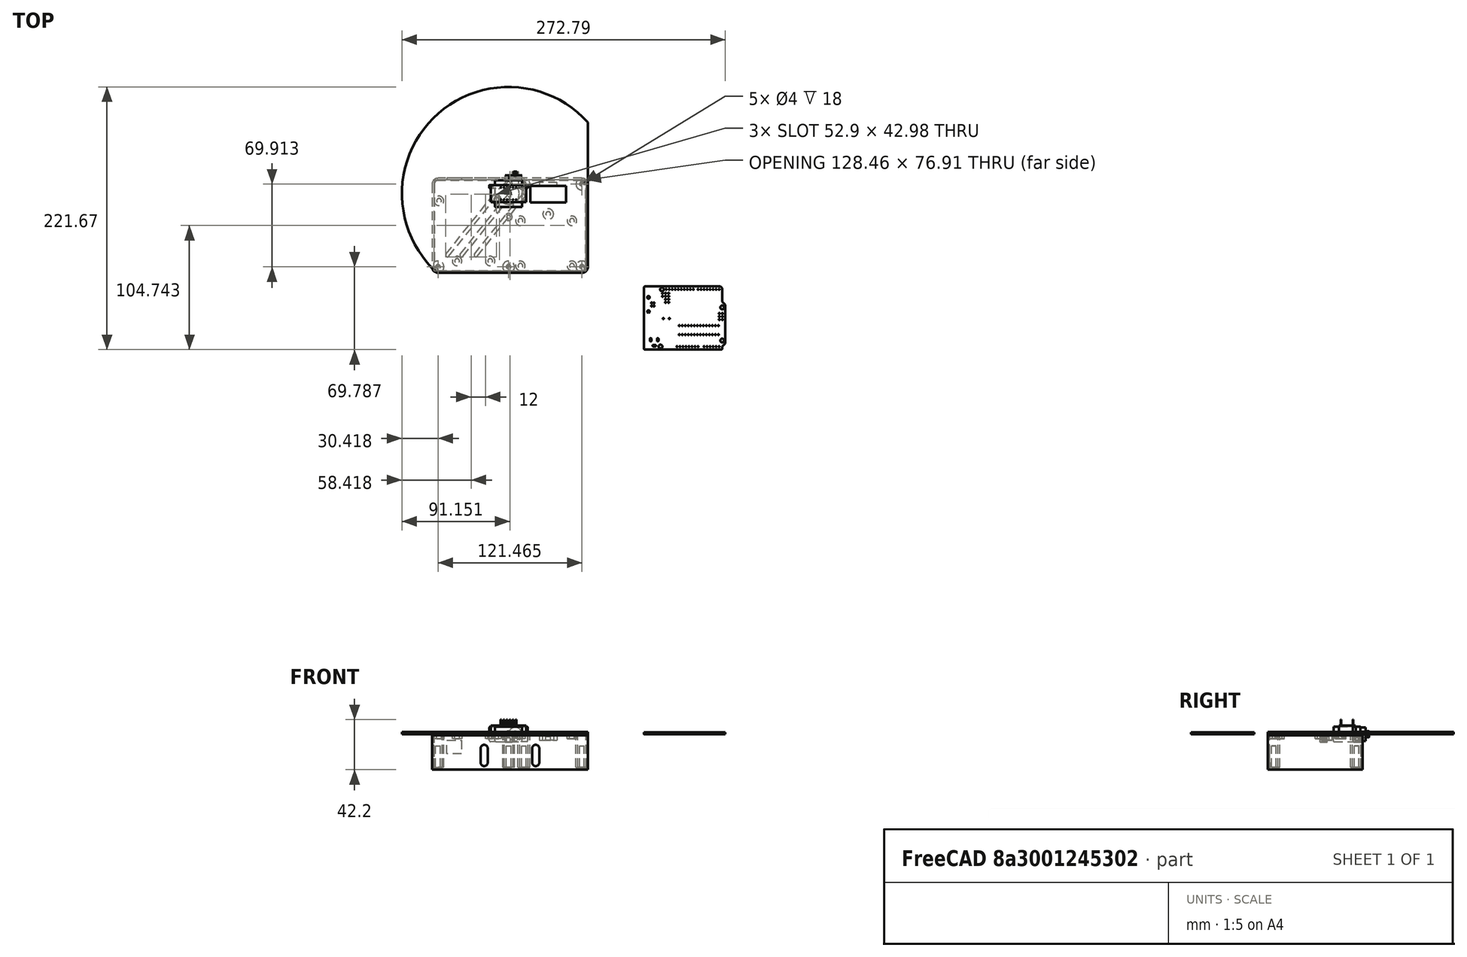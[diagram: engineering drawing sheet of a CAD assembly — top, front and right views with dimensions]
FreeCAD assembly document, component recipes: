
FREECAD ASSEMBLY — COMPONENT RECIPES ("shell")

This assembly document has 4 components, labeled P0..P3 below (a component is one placed body or linked part). 1 of them carries a construction recipe — the FreeCAD feature program that regenerates the part from scratch, quoted from this document or its linked companion documents; the rest are supplied as boundary geometry only. No exploded tour is included for this assembly.
COMPONENT P0 — geometry summary ("Corps001"; no construction recipe available for this part):
  bounding box: 30.0 x 14.0 x 12.2 mm
  tessellated surface: 924 triangles
  volume: 3034 mm^3 (59% of its bounding box)
  symmetry: 2-fold rotationally symmetric about the z axis; mirror-symmetric across its x mid-plane, y mid-plane
COMPONENT P1 — geometry summary ("SG90-SERVO001"; no construction recipe available for this part):
  bounding box: 32.2 x 29.8 x 12.5 mm
  tessellated surface: 14,478 triangles
  volume: 7213 mm^3 (60% of its bounding box)
  symmetry: mirror-symmetric across its x mid-plane
COMPONENT P2 — geometry summary ("UNO-TH_Rev3e_PCB001"; no construction recipe available for this part):
  bounding box: 68.7 x 53.6 x 1.5 mm
  tessellated surface: 16,748 triangles
  volume: 5303 mm^3 (95% of its bounding box)
  symmetry: mirror-symmetric across its z mid-plane
COMPONENT P3 — recipe-attached ("shell001", modeled in this document).
Construction recipe (the document's own serialized feature program — sketch geometry with constraints, then the solid features built on it; lengths are millimeters unless a unit is written):

FEATURE [Sketcher::SketchObject] Sketch
  ArcFitTolerance = 1e-06
  AttachmentSupport = -> [XY_Plane]
  FullyConstrained = true
  MakeInternals = false
  MapMode = 5
  sketch-geometry (14):
    g0: LineSegment StartX=18.4415 StartY=6.5 StartZ=0 EndX=18.4415 EndY=-7.5 EndZ=0
    g1: LineSegment StartX=18.4415 StartY=-7.5 StartZ=0 EndX=48.4415 EndY=-7.5 EndZ=0
    g2: LineSegment StartX=48.4415 StartY=-7.5 StartZ=0 EndX=48.4415 EndY=6.5 EndZ=0
    g3: LineSegment StartX=48.4415 StartY=6.5 StartZ=0 EndX=18.4415 EndY=6.5 EndZ=0
    g4: GeomPoint [constr] X=33.4415 Y=-0.5 Z=0
    g5: ArcOfCircle CenterX=0 CenterY=0 CenterZ=0 NormalX=0 NormalY=0 NormalZ=1 AngleXU=0 Radius=90 StartAngle=0.733038 EndAngle=3.97935
    g6: Circle CenterX=0 CenterY=0 CenterZ=0 NormalX=0 NormalY=0 NormalZ=1 AngleXU=0 Radius=2.5
    g7: LineSegment [constr] StartX=0 StartY=0 StartZ=0 EndX=66.883 EndY=60.2218 EndZ=0
    g8: LineSegment [constr] StartX=0 StartY=0 StartZ=0 EndX=-60.2218 EndY=-66.883 EndZ=0
    g9: LineSegment StartX=66.883 StartY=60.2218 StartZ=0 EndX=66.883 EndY=-61.883 EndZ=0
    g10: LineSegment StartX=61.883 StartY=-66.883 StartZ=0 EndX=-60.2218 EndY=-66.883 EndZ=0
    g11: ArcOfCircle CenterX=61.883 CenterY=-61.883 CenterZ=0 NormalX=0 NormalY=0 NormalZ=1 AngleXU=0 Radius=5 StartAngle=4.71239 EndAngle=6.28319
    g12: LineSegment [constr] StartX=48.4415 StartY=3.78 StartZ=0 EndX=66.883 EndY=3.78 EndZ=0
    g13: LineSegment [constr] StartX=0 StartY=0 StartZ=0 EndX=18.4415 EndY=0 EndZ=0
  constraints (37):
    c: Coincident(g0,g1)
    c: Coincident(g1,g2)
    c: Coincident(g2,g3)
    c: Coincident(g3,g0)
    c: Vertical(g2)
    c: Horizontal(g1)
    c: Horizontal(g3)
    c: Symmetric(g2,g0,g4)
    c: DistanceX(g1,g1) = 30
    c: DistanceY(g2,g2) = 14
    c: Radius(g5) = 90
    c: Coincident(g5,g-1)
    c: Coincident(g6,g5)
    c: Diameter(g6) = 5
    c: Coincident(g7,g5)
    c: Coincident(g8,g5)
    c: Angle(g8,g-1,g5) = 2.30383
    c: Vertical(g9)
    c: Horizontal(g10)
    c: Angle(g-1,g7) = 0.733038
    c: Tangent(g9,g11) = 1.5708
    c: Tangent(g10,g11) = 1.5708
    c: Radius(g11) = 5
    c: Coincident(g5,g8)
    c: Coincident(g5,g7)
    c: Coincident(g9,g5)
    c: Coincident(g10,g5)
    c: PointOnObject(g12,g9)
    c: PointOnObject(g12,g2)
    c: DistanceY(g-1,g12) = 3.78
    c: Horizontal(g12,g12)
    c: Coincident(g13,g5)
    c: Vertical(g13,g0)
    c: PointOnObject(g13,g-1)
    c: Equal(g12,g13)
    c: Perpendicular(g0,g1)
    c: DistanceY(g-1,g4) = -0.5
FEATURE [PartDesign::Pad] Pad  label="BaseFace"
  Direction = (0,0,1)
  Length = 2
  Length2 = 10
  Profile = -> Sketch
  ReferenceAxis = -> Sketch [N_Axis]
  Refine = true
  Suppressed = false
  Type = 0
FEATURE [Sketcher::SketchObject] Sketch001
  ArcFitTolerance = 1e-06
  AttachmentSupport = -> [XY_Plane]
  FullyConstrained = true
  MakeInternals = false
  MapMode = 2
  sketch-geometry (1):
    g0: Circle CenterX=0 CenterY=0 CenterZ=0 NormalX=0 NormalY=0 NormalZ=1 AngleXU=0 Radius=9
  constraints (2):
    c: Diameter(g0) = 18
    c: Coincident(g0,g-1)
FEATURE [Sketcher::SketchObject] Sketch003
  ArcFitTolerance = 1e-06
  AttachmentOffset = pos=(0,0,2) rot=(0,0,1;0rad)
  AttachmentSupport = -> [XY_Plane]
  FullyConstrained = true
  MakeInternals = false
  MapMode = 5
  Placement = pos=(0,0,2) rot=(0,0,1;0rad)
  expr: .AttachmentOffset.Base.z = <<BaseFace>>.Length
  sketch-geometry (3):
    g0: Circle CenterX=0 CenterY=-19.72 CenterZ=0 NormalX=0 NormalY=0 NormalZ=1 AngleXU=0 Radius=3
    g1: Circle CenterX=0 CenterY=8.53 CenterZ=0 NormalX=0 NormalY=0 NormalZ=1 AngleXU=0 Radius=3
    g2: LineSegment [constr] StartX=0 StartY=-19.72 StartZ=0 EndX=0 EndY=8.53 EndZ=0
  constraints (8):
    c: Diameter(g0) = 6
    c: Diameter(g1) = 6
    c: Distance(g0,g1) = 28.25
    c: Distance(g1,g-1) = 8.53
    c: Coincident(g2,g0)
    c: Coincident(g2,g1)
    c: PointOnObject(g-1,g2)
    c: PointOnObject(g0,g-2)
FEATURE [PartDesign::Pocket] Pocket001  label="PocketServo"
  BaseFeature = -> Pad
  Direction = (0,0,-1)
  Length = 1.5
  Length2 = 5
  Profile = -> Sketch001
  ReferenceAxis = -> Sketch001 [N_Axis]
  Refine = true
  Reversed = true
  Suppressed = false
  Type = 0
FEATURE [Sketcher::SketchObject] Sketch002
  ArcFitTolerance = 1e-06
  AttachmentSupport = -> [XY_Plane]
  ExternalGeometry = -> [Pocket001]
  FullyConstrained = true
  MakeInternals = false
  MapMode = 5
  sketch-geometry (5):
    g0: Circle CenterX=-43.4418 CenterY=-56.923 CenterZ=0 NormalX=0 NormalY=0 NormalZ=1 AngleXU=0 Radius=4
    g1: Circle CenterX=-15.5018 CenterY=-56.923 CenterZ=0 NormalX=0 NormalY=0 NormalZ=1 AngleXU=0 Radius=4
    g2: Circle CenterX=-10.4218 CenterY=-4.85303 CenterZ=0 NormalX=0 NormalY=0 NormalZ=1 AngleXU=0 Radius=4
    g3: Circle CenterX=-58.6818 CenterY=-6.12303 CenterZ=0 NormalX=0 NormalY=0 NormalZ=1 AngleXU=0 Radius=4
    g4: GeomPoint X=-61.2218 Y=9.11697 Z=0
  constraints (14):
    c: Equal(g1,g0)
    c: Equal(g0,g3)
    c: Equal(g3,g2)
    c: Diameter(g3) = 8
    c: DistanceY(g4,g3) = -15.24
    c: DistanceY(g4,g0) = -66.04
    c: Horizontal(g0,g1)
    c: DistanceX(g4,g3) = 2.54
    c: DistanceX(g4,g2) = 50.8
    c: DistanceX(g4,g0) = 17.78
    c: DistanceX(g4,g1) = 45.72
    c: DistanceX(g4,g-3) = 1
    c: DistanceY(g4,g-3) = -76
    c: DistanceY(g4,g2) = -13.97
FEATURE [PartDesign::Pad] Pad005  label="PadArduino"
  BaseFeature = -> Pocket001
  Direction = (0,0,1)
  Length = 4
  Length2 = 10
  Profile = -> Sketch002
  ReferenceAxis = -> Sketch002 [N_Axis]
  Refine = true
  Reversed = true
  Suppressed = false
  Type = 0
FEATURE [PartDesign::Pad] Pad002  label="PadServo"
  BaseFeature = -> Pad005
  Direction = (0,0,1)
  Length = 8.75
  Length2 = 10
  Profile = -> Sketch003
  ReferenceAxis = -> Sketch003 [N_Axis]
  Refine = true
  Reversed = true
  Suppressed = false
  Type = 0
  expr: Length = 6.75 mm + <<BaseFace>>.Length
FEATURE [Sketcher::SketchObject] Sketch004
  ArcFitTolerance = 1e-06
  AttachmentSupport = -> [XY_Plane003]
  ExternalGeometry = -> [Pad002]
  FullyConstrained = true
  MakeInternals = false
  MapMode = 5
  sketch-geometry (16):
    g0: LineSegment StartX=61.883 StartY=11.53 StartZ=0 EndX=-59.5818 EndY=11.53 EndZ=0
    g1: LineSegment StartX=-63.0818 StartY=8.03 StartZ=0 EndX=-63.0818 EndY=-61.883 EndZ=0
    g2: LineSegment StartX=-59.5818 StartY=-65.383 StartZ=0 EndX=61.883 EndY=-65.383 EndZ=0
    g3: LineSegment StartX=65.383 StartY=-61.883 StartZ=0 EndX=65.383 EndY=8.03 EndZ=0
    g4: ArcOfCircle CenterX=61.883 CenterY=8.03 CenterZ=0 NormalX=0 NormalY=0 NormalZ=1 AngleXU=0 Radius=3.5 StartAngle=1e-16 EndAngle=1.5708
    g5: ArcOfCircle CenterX=-59.5818 CenterY=8.03 CenterZ=0 NormalX=0 NormalY=0 NormalZ=1 AngleXU=0 Radius=3.5 StartAngle=1.5708 EndAngle=3.14159
    g6: ArcOfCircle CenterX=-59.5818 CenterY=-61.883 CenterZ=0 NormalX=0 NormalY=0 NormalZ=1 AngleXU=0 Radius=3.5 StartAngle=3.14159 EndAngle=4.71239
    g7: ArcOfCircle CenterX=61.883 CenterY=-61.883 CenterZ=0 NormalX=0 NormalY=0 NormalZ=1 AngleXU=0 Radius=3.5 StartAngle=4.71239 EndAngle=6.28319
    g8: LineSegment StartX=61.883 StartY=13.03 StartZ=0 EndX=-59.5818 EndY=13.03 EndZ=0
    g9: LineSegment StartX=-64.5818 StartY=8.03 StartZ=0 EndX=-64.5818 EndY=-61.883 EndZ=0
    g10: LineSegment StartX=-59.5818 StartY=-66.883 StartZ=0 EndX=61.883 EndY=-66.883 EndZ=0
    g11: LineSegment StartX=66.883 StartY=-61.883 StartZ=0 EndX=66.883 EndY=8.03 EndZ=0
    g12: ArcOfCircle CenterX=61.883 CenterY=8.03 CenterZ=0 NormalX=0 NormalY=0 NormalZ=1 AngleXU=0 Radius=5 StartAngle=0 EndAngle=1.5708
    g13: ArcOfCircle CenterX=-59.5818 CenterY=8.03 CenterZ=0 NormalX=0 NormalY=0 NormalZ=1 AngleXU=0 Radius=5 StartAngle=1.5708 EndAngle=3.14159
    g14: ArcOfCircle CenterX=-59.5818 CenterY=-61.883 CenterZ=0 NormalX=0 NormalY=0 NormalZ=1 AngleXU=0 Radius=5 StartAngle=3.14159 EndAngle=4.71239
    g15: ArcOfCircle CenterX=61.883 CenterY=-61.883 CenterZ=0 NormalX=0 NormalY=0 NormalZ=1 AngleXU=0 Radius=5 StartAngle=4.71239 EndAngle=6.28319
  constraints (38):
    c: Tangent(g0,g4) = -1.5708
    c: Tangent(g0,g5) = -1.5708
    c: Tangent(g1,g5) = -1.5708
    c: Tangent(g1,g6) = -1.5708
    c: Tangent(g2,g6) = -1.5708
    c: Tangent(g2,g7) = -1.5708
    c: Tangent(g3,g7) = -1.5708
    c: Tangent(g3,g4) = -1.5708
    c: Horizontal(g0)
    c: Horizontal(g2)
    c: Vertical(g1)
    c: Vertical(g3)
    c: Equal(g4,g5)
    c: Equal(g5,g6)
    c: Equal(g6,g7)
    c: Tangent(g8,g12) = -1.5708
    c: Tangent(g8,g13) = -1.5708
    c: Tangent(g9,g13) = -1.5708
    c: Tangent(g9,g14) = -1.5708
    c: Tangent(g10,g14) = -1.5708
    c: Tangent(g10,g15) = -1.5708
    c: Tangent(g11,g15) = -1.5708
    c: Tangent(g11,g12) = -1.5708
    c: Horizontal(g8)
    c: Vertical(g9)
    c: Equal(g12,g13)
    c: Equal(g13,g14)
    c: Equal(g14,g15)
    c: Distance(g10,g2) = 1.5
    c: Vertical(g0,g8)
    c: Horizontal(g3,g11)
    c: Vertical(g8,g0)
    c: Distance(g0,g8) = 1.5
    c: Tangent(g11,g-6)
    c: Distance(g5,g13) = 5
    c: Tangent(g-5,g10)
    c: Tangent(g0,g-3)
    c: Distance(g-4,g1) = 0.4
FEATURE [PartDesign::Pad] Pad006  label="PadContour"
  BaseFeature = -> Pad002
  Direction = (0,0,1)
  Length = 30
  Length2 = 10
  Profile = -> Sketch004
  ReferenceAxis = -> Sketch004 [N_Axis]
  Refine = true
  Reversed = true
  Suppressed = false
  Type = 0
FEATURE [Sketcher::SketchObject] Sketch005
  ArcFitTolerance = 1e-06
  ExternalGeometry = -> [Sketch002]
  FullyConstrained = true
  MakeInternals = false
  MapMode = 5
  Placement = pos=(0,12.03,0) rot=(0,0.707107,0.707107;3.14159rad)
  sketch-geometry (4):
    g0: LineSegment StartX=52.1718 StartY=-16.66 StartZ=0 EndX=52.1718 EndY=-5.26 EndZ=0
    g1: LineSegment StartX=52.1718 StartY=-5.26 StartZ=0 EndX=39.6718 EndY=-5.26 EndZ=0
    g2: LineSegment StartX=39.6718 StartY=-5.26 StartZ=0 EndX=39.6718 EndY=-16.66 EndZ=0
    g3: LineSegment StartX=39.6718 StartY=-16.66 StartZ=0 EndX=52.1718 EndY=-16.66 EndZ=0
  constraints (12):
    c: Coincident(g0,g1)
    c: Coincident(g1,g2)
    c: Coincident(g2,g3)
    c: Coincident(g3,g0)
    c: Vertical(g0)
    c: Vertical(g2)
    c: Horizontal(g1)
    c: Horizontal(g3)
    c: DistanceY(g1,g-3) = 5.26
    c: DistanceX(g0,g-3) = 9.05
    c: DistanceX(g1,g1) = 12.5
    c: DistanceY(g2,g2) = 11.4
FEATURE [PartDesign::Pocket] Pocket  label="PocketUSB"
  BaseFeature = -> Pad006
  Direction = (-1e-16,-1,2e-16)
  Length = 5
  Length2 = 5
  Profile = -> Sketch005
  ReferenceAxis = -> Sketch005 [N_Axis]
  Refine = true
  Reversed = true
  Suppressed = false
  Type = 4
FEATURE [Sketcher::SketchObject] Sketch006
  ArcFitTolerance = 1e-06
  AttachmentSupport = -> [XY_Plane]
  ExternalGeometry = -> [Pocket]
  FullyConstrained = true
  MakeInternals = false
  MapMode = 5
  sketch-geometry (6):
    g0: Circle CenterX=33.4415 CenterY=-17.25 CenterZ=0 NormalX=0 NormalY=0 NormalZ=1 AngleXU=0 Radius=4.5
    g1: LineSegment StartX=40.9415 StartY=9.3 StartZ=0 EndX=25.9415 EndY=9.3 EndZ=0
    g2: LineSegment StartX=25.9415 StartY=9.3 StartZ=0 EndX=25.9415 EndY=6.5 EndZ=0
    g3: LineSegment StartX=25.9415 StartY=6.5 StartZ=0 EndX=40.9415 EndY=6.5 EndZ=0
    g4: LineSegment StartX=40.9415 StartY=6.5 StartZ=0 EndX=40.9415 EndY=9.3 EndZ=0
    g5: GeomPoint [constr] X=33.4415 Y=7.9 Z=0
  constraints (16):
    c: Diameter(g0) = 9
    c: Distance(g0,g-3) = 23.75
    c: Coincident(g1,g2)
    c: Coincident(g2,g3)
    c: Coincident(g3,g4)
    c: Coincident(g4,g1)
    c: Horizontal(g3)
    c: Vertical(g2)
    c: Vertical(g4)
    c: Symmetric(g3,g1,g5)
    c: PointOnObject(g2,g-3)
    c: DistanceX(g-3,g5) = 15
    c: Equal(g2,g4)
    c: DistanceY(g2,g1) = 2.8
    c: DistanceX(g1,g1) = 15
    c: DistanceX(g-4,g0) = 15
FEATURE [PartDesign::Pad] Pad007
  BaseFeature = -> Pocket
  Direction = (0,0,1)
  Length = 5
  Length2 = 10
  Profile = -> Sketch006
  ReferenceAxis = -> Sketch006 [N_Axis]
  Refine = true
  Reversed = true
  Suppressed = false
  Type = 0
FEATURE [PartDesign::Hole] Hole002  label="HoleDigits"
  BaseFeature = -> Pad007
  CustomThreadClearance = 0
  Depth = 3
  DepthType = 0
  Diameter = 4
  DrillForDepth = false
  DrillPoint = 0
  DrillPointAngle = 118
  HoleCutCountersinkAngle = 90
  HoleCutCustomValues = false
  HoleCutDepth = 0
  HoleCutDiameter = 6.1
  HoleCutType = 0
  ModelThread = false
  Profile = -> Pad007 [Face49]
  Refine = true
  Suppressed = false
  Tapered = false
  TaperedAngle = 90
  ThreadClass = 0
  ThreadDepth = 3
  ThreadDepthType = 0
  ThreadDirection = 0
  ThreadFit = 0
  ThreadSize = 0
  ThreadType = 0
  Threaded = false
  UseCustomThreadClearance = false
FEATURE [Sketcher::SketchObject] Sketch007
  ArcFitTolerance = 1e-06
  FullyConstrained = true
  MakeInternals = false
  Placement = pos=(0,0,0) rot=(1,0,0;3.14159rad)
  sketch-geometry (7):
    g0: Circle CenterX=53.5 CenterY=61 CenterZ=0 NormalX=0 NormalY=0 NormalZ=1 AngleXU=0 Radius=4
    g1: Circle CenterX=10 CenterY=23 CenterZ=0 NormalX=0 NormalY=0 NormalZ=1 AngleXU=0 Radius=4
    g2: Circle CenterX=53.5 CenterY=23 CenterZ=0 NormalX=0 NormalY=0 NormalZ=1 AngleXU=0 Radius=4
    g3: Circle CenterX=10 CenterY=61 CenterZ=0 NormalX=0 NormalY=0 NormalZ=1 AngleXU=0 Radius=4
    g4: LineSegment [constr] StartX=10 StartY=61 StartZ=0 EndX=53.5 EndY=61 EndZ=0
    g5: LineSegment [constr] StartX=10 StartY=23 StartZ=0 EndX=53.5 EndY=23 EndZ=0
    g6: LineSegment [constr] StartX=53.5 StartY=23 StartZ=0 EndX=53.5 EndY=61 EndZ=0
  constraints (18):
    c: Equal(g3,g0)
    c: Equal(g0,g2)
    c: Equal(g2,g1)
    c: Diameter(g3) = 8
    c: Coincident(g4,g3)
    c: Coincident(g4,g0)
    c: Coincident(g5,g1)
    c: Coincident(g5,g2)
    c: Coincident(g6,g2)
    c: Coincident(g6,g0)
    c: Vertical(g6)
    c: Horizontal(g4)
    c: Horizontal(g5)
    c: Equal(g5,g4)
    c: DistanceX(g4,g4) = 43.5
    c: DistanceY(g6,g6) = 38
    c: DistanceY(g-1,g1) = 23
    c: DistanceX(g-1,g1) = 10
FEATURE [PartDesign::Pad] Pad008
  BaseFeature = -> Hole002
  Direction = (0,-1e-16,-1)
  Length = 4
  Length2 = 10
  Profile = -> Sketch007
  ReferenceAxis = -> Sketch007 [N_Axis]
  Refine = true
  Suppressed = false
  Type = 0
FEATURE [PartDesign::Hole] Hole  label="HoleMainBoard"
  BaseFeature = -> Pad008
  CustomThreadClearance = 0
  Depth = 4
  DepthType = 0
  Diameter = 4
  DrillForDepth = false
  DrillPoint = 0
  DrillPointAngle = 118
  HoleCutCountersinkAngle = 90
  HoleCutCustomValues = false
  HoleCutDepth = 0
  HoleCutDiameter = 6.1
  HoleCutType = 0
  ModelThread = false
  Profile = -> Pad008 [Face53,Face61,Face58,Face52]
  Refine = true
  Suppressed = false
  Tapered = false
  TaperedAngle = 90
  ThreadClass = 0
  ThreadDepth = 4
  ThreadDepthType = 0
  ThreadDirection = 0
  ThreadFit = 0
  ThreadSize = 0
  ThreadType = 0
  Threaded = false
  UseCustomThreadClearance = false
FEATURE [PartDesign::Hole] Hole003  label="HoleUNO"
  BaseFeature = -> Hole
  CustomThreadClearance = 0
  Depth = 4
  DepthType = 0
  Diameter = 4
  DrillForDepth = false
  DrillPoint = 0
  DrillPointAngle = 118
  HoleCutCountersinkAngle = 90
  HoleCutCustomValues = false
  HoleCutDepth = 0
  HoleCutDiameter = 6.1
  HoleCutType = 0
  ModelThread = false
  Profile = -> Hole [Face54,Face50,Face51,Face57]
  Refine = true
  Suppressed = false
  Tapered = false
  TaperedAngle = 90
  ThreadClass = 0
  ThreadDepth = 4
  ThreadDepthType = 0
  ThreadDirection = 0
  ThreadFit = 0
  ThreadSize = 0
  ThreadType = 0
  Threaded = false
  UseCustomThreadClearance = false
FEATURE [Sketcher::SketchObject] Sketch008
  ArcFitTolerance = 1e-06
  AttachmentSupport = -> [XY_Plane]
  ExternalGeometry = -> [Hole003]
  FullyConstrained = true
  MakeInternals = false
  MapMode = 5
  Placement = pos=(0,0,0) rot=(0,1,0;3.14159rad)
  sketch-geometry (5):
    g0: Circle CenterX=-61.883 CenterY=8.03 CenterZ=0 NormalX=0 NormalY=0 NormalZ=1 AngleXU=0 Radius=5
    g1: Circle CenterX=59.5818 CenterY=-61.883 CenterZ=0 NormalX=0 NormalY=0 NormalZ=1 AngleXU=0 Radius=5
    g2: Circle CenterX=-61.883 CenterY=-61.883 CenterZ=0 NormalX=0 NormalY=0 NormalZ=1 AngleXU=0 Radius=5
    g3: Circle CenterX=0 CenterY=-61.883 CenterZ=0 NormalX=0 NormalY=0 NormalZ=1 AngleXU=0 Radius=5
    g4: Circle CenterX=-13 CenterY=8.03 CenterZ=0 NormalX=0 NormalY=0 NormalZ=1 AngleXU=0 Radius=5
  constraints (15):
    c: Equal(g2,g3)
    c: Equal(g3,g0)
    c: Diameter(g0) = 10
    c: Tangent(g1,g-6)
    c: Tangent(g0,g-3)
    c: Tangent(g0,g-4)
    c: PointOnObject(g3,g-2)
    c: Tangent(g3,g-5)
    c: Tangent(g2,g-5)
    c: Tangent(g2,g-4)
    c: Diameter(g1) = 10
    c: Tangent(g1,g-5)
    c: Equal(g0,g4)
    c: Tangent(g4,g-3)
    c: Distance(g4,g-2) = 13
FEATURE [PartDesign::Pad] Pad009
  BaseFeature = -> Hole003
  Direction = (0,0,-1)
  Length = 28
  Length2 = 10
  Profile = -> Sketch008
  ReferenceAxis = -> Sketch008 [N_Axis]
  Refine = true
  Suppressed = false
  Type = 0
FEATURE [PartDesign::Hole] Hole004
  BaseFeature = -> Pad009
  CustomThreadClearance = 0
  Depth = 4
  DepthType = 0
  Diameter = 3.2
  DrillForDepth = false
  DrillPoint = 0
  DrillPointAngle = 118
  HoleCutCountersinkAngle = 90
  HoleCutCustomValues = false
  HoleCutDepth = 0
  HoleCutDiameter = 6.1
  HoleCutType = 0
  ModelThread = false
  Profile = -> Pad002 [Face19,Face22]
  Refine = true
  Suppressed = false
  Tapered = false
  TaperedAngle = 90
  ThreadClass = 0
  ThreadDepth = 4
  ThreadDepthType = 0
  ThreadDirection = 0
  ThreadFit = 0
  ThreadSize = 0
  ThreadType = 0
  Threaded = false
  UseCustomThreadClearance = false
FEATURE [PartDesign::Hole] Hole005
  BaseFeature = -> Hole004
  CustomThreadClearance = 0
  Depth = 18
  DepthType = 0
  Diameter = 4
  DrillForDepth = false
  DrillPoint = 0
  DrillPointAngle = 118
  HoleCutCountersinkAngle = 90
  HoleCutCustomValues = false
  HoleCutDepth = 0
  HoleCutDiameter = 6.1
  HoleCutType = 0
  ModelThread = false
  Profile = -> Hole004 [Face42,Face44,Face40,Face37,Face46]
  Refine = true
  Suppressed = false
  Tapered = false
  TaperedAngle = 90
  ThreadClass = 0
  ThreadDepth = 18
  ThreadDepthType = 0
  ThreadDirection = 0
  ThreadFit = 0
  ThreadSize = 0
  ThreadType = 0
  Threaded = false
  UseCustomThreadClearance = false
FEATURE [Sketcher::SketchObject] Sketch010
  ArcFitTolerance = 1e-06
  AttachmentSupport = -> [Hole005]
  ExternalGeometry = -> [Hole005]
  FullyConstrained = true
  MakeInternals = false
  MapMode = 5
  Placement = pos=(0,-66.883,0) rot=(1,0,0;1.5708rad)
  sketch-geometry (8):
    g0: ArcOfCircle CenterX=22.883 CenterY=-24 CenterZ=0 NormalX=0 NormalY=0 NormalZ=1 AngleXU=0 Radius=3 StartAngle=3.14159 EndAngle=6.28319
    g1: ArcOfCircle CenterX=22.883 CenterY=-12 CenterZ=0 NormalX=0 NormalY=0 NormalZ=1 AngleXU=0 Radius=3 StartAngle=1e-16 EndAngle=3.14159
    g2: LineSegment StartX=19.883 StartY=-24 StartZ=0 EndX=19.883 EndY=-12 EndZ=0
    g3: LineSegment StartX=25.883 StartY=-24 StartZ=0 EndX=25.883 EndY=-12 EndZ=0
    g4: ArcOfCircle CenterX=-20.5818 CenterY=-24 CenterZ=0 NormalX=0 NormalY=0 NormalZ=1 AngleXU=0 Radius=3 StartAngle=3.14159 EndAngle=6.28319
    g5: ArcOfCircle CenterX=-20.5818 CenterY=-12 CenterZ=0 NormalX=0 NormalY=0 NormalZ=1 AngleXU=0 Radius=3 StartAngle=3.35329e-11 EndAngle=3.14159
    g6: LineSegment StartX=-23.5818 StartY=-24 StartZ=0 EndX=-23.5818 EndY=-12 EndZ=0
    g7: LineSegment StartX=-17.5818 StartY=-24 StartZ=0 EndX=-17.5818 EndY=-12 EndZ=0
  constraints (20):
    c: Tangent(g0,g2) = 1.5708
    c: Tangent(g0,g3) = -1.5708
    c: Tangent(g1,g2) = 1.5708
    c: Tangent(g1,g3) = -1.5708
    c: Equal(g0,g1)
    c: Radius(g0) = 3
    c: Vertical(g2)
    c: Tangent(g4,g6) = 1.5708
    c: Tangent(g4,g7) = -1.5708
    c: Tangent(g5,g6) = 1.5708
    c: Tangent(g5,g7) = -1.5708
    c: Equal(g4,g5)
    c: Radius(g4) = 3
    c: Vertical(g6)
    c: Horizontal(g5,g1)
    c: Horizontal(g4,g0)
    c: Distance(g1,g-4) = 39
    c: Distance(g5,g-5) = 39
    c: Distance(g5,g-3) = 14
    c: DistanceY(g7,g7) = 12
FEATURE [PartDesign::Pocket] Pocket003
  BaseFeature = -> Hole005
  Direction = (0,1,-2e-16)
  Length = 5
  Length2 = 5
  Profile = -> Sketch010
  ReferenceAxis = -> Sketch010 [N_Axis]
  Refine = true
  Suppressed = false
  Type = 0
FEATURE [PartDesign::Body] Body  label="shell"
  AllowCompound = false
  Group = -> [Sketch,Pad,Sketch001,Pocket001,Sketch002,Pad005,Pad002,Sketch003,Sketch004,Pad006,Sketch005,Pocket,Sketch006,Pad007,Hole002,Sketch007,Pad008,Hole,Hole003,Sketch008,Pad009,Hole004,Hole005,Sketch010,Pocket003]
  Origin = -> Origin
  Tip = -> Pocket003
PROVENANCE & LICENSES
A FreeCAD (.FCStd) document from a public repository crawl; recipes are the document's own serialized feature recipes (and, for linked parts, companion documents' recipes).
License: as declared in the source repository (recorded in the dataset sidecar).
